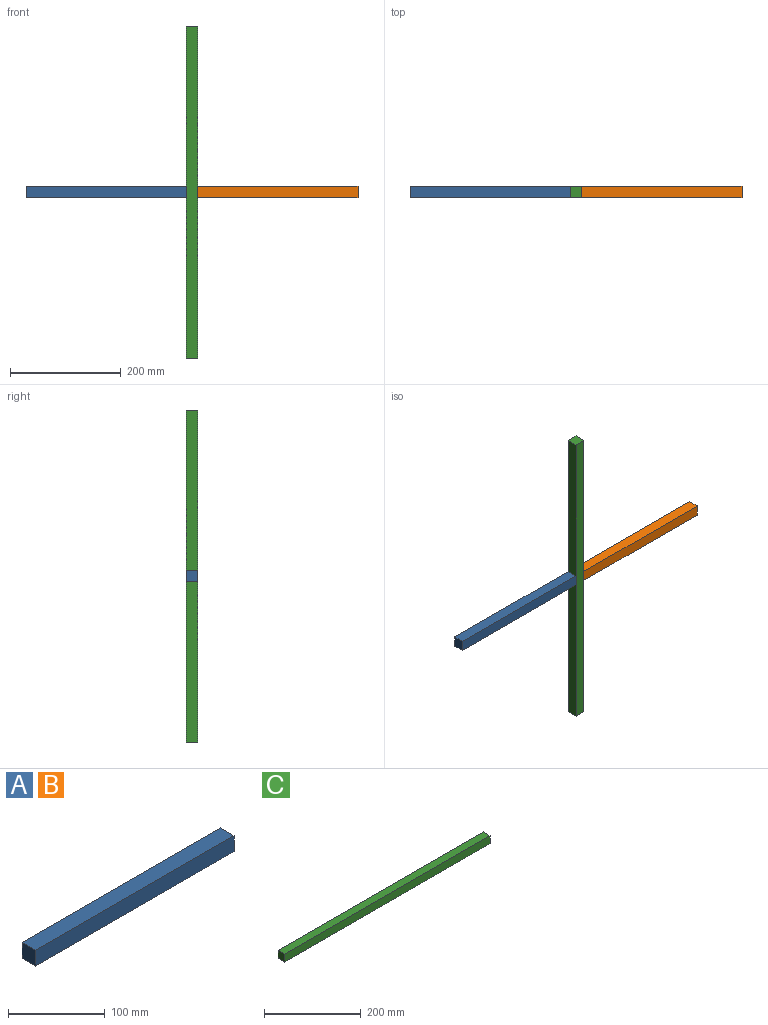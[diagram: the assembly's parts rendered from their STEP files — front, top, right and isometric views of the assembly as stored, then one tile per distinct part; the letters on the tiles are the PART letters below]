
ASSEMBLY  parts=3 mates=2
PART A: 6 faces, bbox 290x20x20 mm
  f0: plane 290x20mm, normal (0,0,1), area 5800mm2, adj f1,f3,f4,f5
  f1: plane 20x20mm, normal (-1,0,0), area 400mm2, adj f0,f2,f4,f5
  f2: plane 290x20mm, normal (0,0,-1), area 5800mm2, adj f1,f3,f4,f5
  f3: plane 20x20mm, normal (1,0,0), area 400mm2, adj f0,f2,f4,f5
  f4: plane 290x20mm, normal (0,-1,0), area 5800mm2, adj f0,f1,f2,f3
  f5: plane 290x20mm, normal (0,1,0), area 5800mm2, adj f0,f1,f2,f3
PART B: same geometry as A
PART C: 6 faces, bbox 600x20x20 mm
  f0: plane 600x20mm, normal (0,0,1), area 12000mm2, adj f1,f3,f4,f5
  f1: plane 20x20mm, normal (-1,0,0), area 400mm2, adj f0,f2,f4,f5
  f2: plane 600x20mm, normal (0,0,-1), area 12000mm2, adj f1,f3,f4,f5
  f3: plane 20x20mm, normal (1,0,0), area 400mm2, adj f0,f2,f4,f5
  f4: plane 600x20mm, normal (0,-1,0), area 12000mm2, adj f0,f1,f2,f3
  f5: plane 600x20mm, normal (0,1,0), area 12000mm2, adj f0,f1,f2,f3
PLACE A t=(-467.54,50.55,93.55)mm
PLACE B t=(-157.54,50.55,93.55)mm
PLACE C rot(axis=(-0.58,0.58,0.58),120deg) t=(-209.2,65.91,98.99)mm
MATE fastened C.f5 <-> A.f3  axis (-1,0,0) through (-209.2,40.55,103.06)mm
MATE fastened C.f4 <-> B.f1  axis (1,0,0) through (-189.2,40.55,103.06)mm
